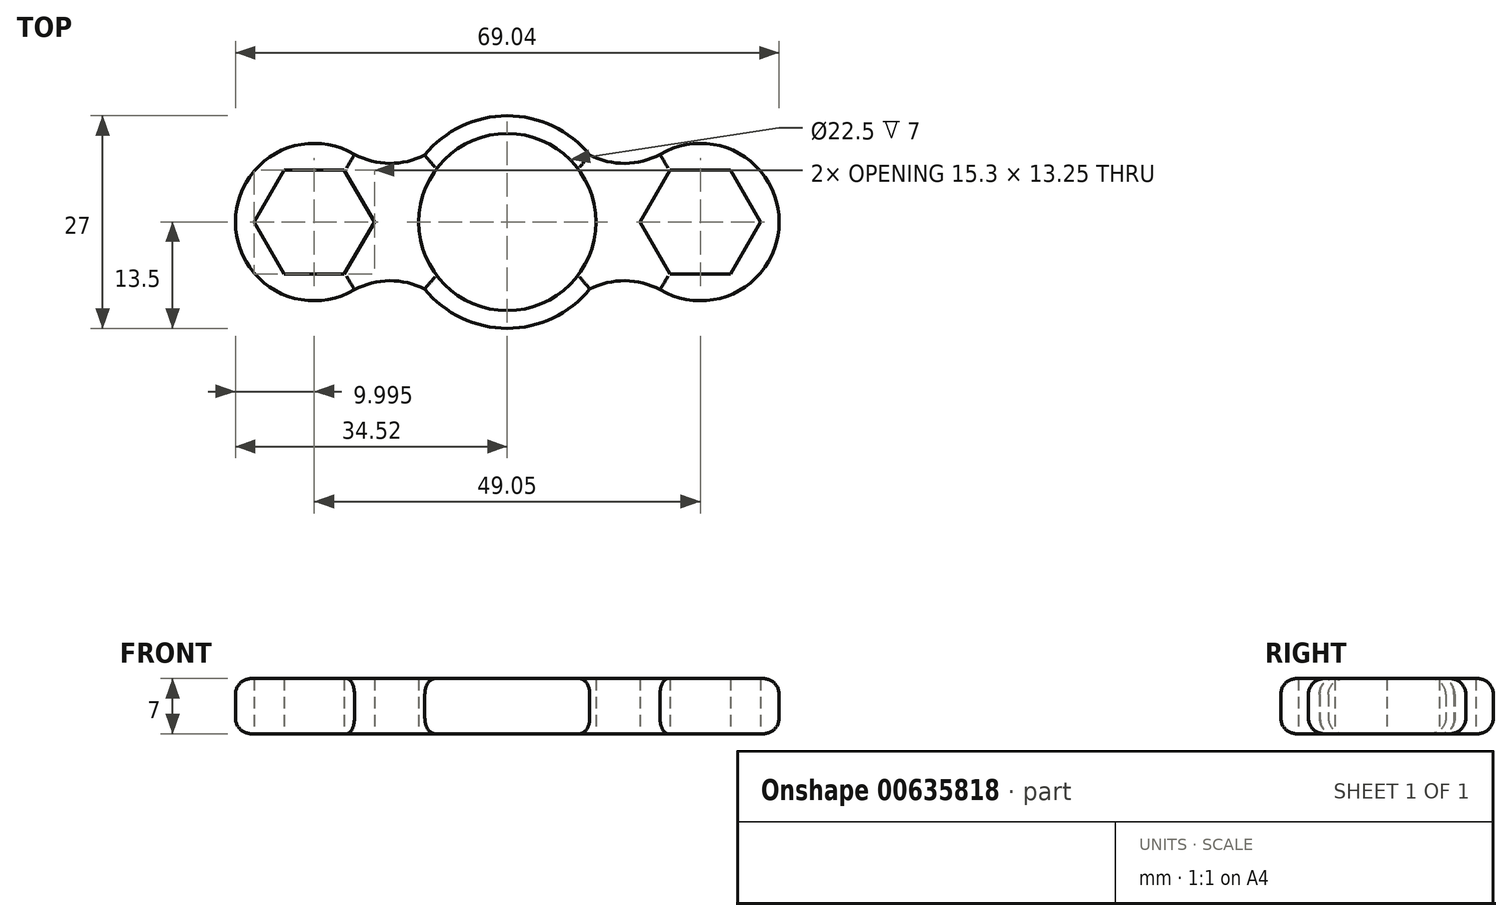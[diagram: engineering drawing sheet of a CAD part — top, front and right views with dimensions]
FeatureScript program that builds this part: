
annotation { "Feature Type Name" : "Feature", "Feature Type Description" : "" }
export const myFeature = defineFeature(function(context is Context, id is Id, definition is map)
    precondition{}
    {
        {
            var Q0;
            Q0=qCreatedBy(makeId("Top.planeOp"),FACE);
            var sketch = newSketch(context, id + "F0", { "sketchPlane" : qUnion([Q0])});
            skCircle(sketch, "E0", {"center": v(0, 0) * mm, "radius": 11.25 * mm});
            skCircle(sketch, "E1", {"center": v(24.52, 0) * mm, "radius": 10 * mm});
            skCircle(sketch, "E2", {"center": v(0, 0) * mm, "radius": 13.5 * mm});
            skPoint(sketch, "E3.center", {"position": v(-1.17, 0) * mm});
            skCircle(sketch, "E4.cCircle", {"center": v(24.52, 0) * mm, "radius": 6.62 * mm, "construction": true});
            skLineSegment(sketch, "E4.0", {"start": v(20.7, 6.63) * mm, "end": v(28.35, 6.63) * mm});
            skLineSegment(sketch, "E4.1", {"start": v(28.35, 6.62) * mm, "end": v(32.17, 0) * mm});
            skLineSegment(sketch, "E4.2", {"start": v(32.17, 0) * mm, "end": v(28.35, -6.62) * mm});
            skLineSegment(sketch, "E4.3", {"start": v(28.35, -6.62) * mm, "end": v(20.7, -6.62) * mm});
            skLineSegment(sketch, "E4.4", {"start": v(20.7, -6.63) * mm, "end": v(16.87, 0) * mm});
            skLineSegment(sketch, "E4.5", {"start": v(16.87, 0) * mm, "end": v(20.7, 6.62) * mm});
            skPoint(sketch, "E4.0.midPoint", {"position": v(24.52, 6.63) * mm});
            skLineSegment(sketch, "E5.MirrorCS", {"start": v(-16.87, 0) * mm, "end": v(-20.7, 6.62) * mm});
            skPoint(sketch, "E6.MirrorP", {"position": v(-24.52, 6.63) * mm});
            skCircle(sketch, "E7.MirrorC", {"center": v(-24.52, 0) * mm, "radius": 10 * mm});
            skCircle(sketch, "E8.MirrorC", {"center": v(-24.52, 0) * mm, "radius": 6.62 * mm, "construction": true});
            skLineSegment(sketch, "E9.MirrorCS", {"start": v(-32.17, 0) * mm, "end": v(-28.35, -6.62) * mm});
            skLineSegment(sketch, "E10.MirrorCS", {"start": v(-28.35, -6.63) * mm, "end": v(-20.7, -6.63) * mm});
            skLineSegment(sketch, "E11.MirrorCS", {"start": v(-20.7, 6.63) * mm, "end": v(-28.35, 6.63) * mm});
            skLineSegment(sketch, "E12.MirrorCS", {"start": v(-28.35, 6.62) * mm, "end": v(-32.17, 0) * mm});
            skLineSegment(sketch, "E13.MirrorCS", {"start": v(-20.7, -6.63) * mm, "end": v(-16.87, 0) * mm});
            skLineSegment(sketch, "E14", {"start": v(0, 0) * mm, "end": v(40.83, 0) * mm, "construction": true});
            skArc(sketch, "E15", {"start": v(19.41, -8.6) * mm, "mid": v(14.95, -7.45) * mm, "end": v(10.48, -8.51) * mm});
            skArc(sketch, "E16.MirrorCS", {"start": v(19.41, 8.6) * mm, "mid": v(14.95, 7.45) * mm, "end": v(10.48, 8.51) * mm});
            skArc(sketch, "E17.MirrorCS", {"start": v(-19.41, 8.6) * mm, "mid": v(-14.95, 7.45) * mm, "end": v(-10.48, 8.51) * mm});
            skArc(sketch, "E18.MirrorCS", {"start": v(-19.41, -8.6) * mm, "mid": v(-14.95, -7.45) * mm, "end": v(-10.48, -8.51) * mm});
            skSolve(sketch);
        }
        {
            var Q0;
            Q0=makeQuery(id+"F0.imprint","IMPRINT",FACE,{"disambiguationData":[TD([[makeQuery(id+"F0.imprint","IMPRINT",EDGE,{"derivedFrom":sQuery(id+"F0.wireOp",EDGE,"E4.0")}),1.0]])]});
            var Q1;
            {var subQ0=sQuery(id+"F0.wireOp",EDGE,"E17.MirrorCS");var subQ1=sQuery(id+"F0.wireOp",EDGE,"E2");var subQ2=makeQuery(id+"F0.imprint","INTERSECT",VERTEX,{"derivedFrom":[subQ1,subQ0]});Q1=makeQuery(id+"F0.imprint","IMPRINT",FACE,{"disambiguationData":[TD([[makeQuery(id+"F0.imprint","IMPRINT",EDGE,{"disambiguationData":[TD([[subQ2,-1.0]])],"derivedFrom":subQ1}),-1.0]])]});}
            var Q2;
            Q2=makeQuery(id+"F0.imprint","IMPRINT",FACE,{"disambiguationData":[TD([[makeQuery(id+"F0.imprint","IMPRINT",EDGE,{"derivedFrom":sQuery(id+"F0.wireOp",EDGE,"E0")}),-1.0]])]});
            var Q3;
            {var subQ0=sQuery(id+"F0.wireOp",EDGE,"E16.MirrorCS");var subQ1=sQuery(id+"F0.wireOp",EDGE,"E1");var subQ2=makeQuery(id+"F0.imprint","INTERSECT",VERTEX,{"disambiguationData":[OD(1.0)],"derivedFrom":[subQ1,subQ0]});Q3=makeQuery(id+"F0.imprint","IMPRINT",FACE,{"disambiguationData":[TD([[makeQuery(id+"F0.imprint","IMPRINT",EDGE,{"disambiguationData":[TD([[subQ2,-1.0]])],"derivedFrom":subQ1}),-1.0]])]});}
            var Q4;
            Q4=makeQuery(id+"F0.imprint","IMPRINT",FACE,{"disambiguationData":[TD([[makeQuery(id+"F0.imprint","IMPRINT",EDGE,{"derivedFrom":sQuery(id+"F0.wireOp",EDGE,"E10.MirrorCS")}),-1.0]])]});
            var Q5;
            {var subQ0=sQuery(id+"F0.wireOp",EDGE,"E16.MirrorCS");var subQ1=sQuery(id+"F0.wireOp",EDGE,"E1");var subQ2=makeQuery(id+"F0.imprint","INTERSECT",VERTEX,{"disambiguationData":[OD(0.0)],"derivedFrom":[subQ1,subQ0]});Q5=makeQuery(id+"F0.imprint","IMPRINT",FACE,{"disambiguationData":[TD([[makeQuery(id+"F0.imprint","IMPRINT",EDGE,{"disambiguationData":[TD([[subQ2,-1.0]])],"derivedFrom":subQ1}),1.0]])]});}
            var Q6;
            {var subQ0=sQuery(id+"F0.wireOp",EDGE,"E15");var subQ1=sQuery(id+"F0.wireOp",EDGE,"E1");var subQ2=makeQuery(id+"F0.imprint","INTERSECT",VERTEX,{"disambiguationData":[OD(0.0)],"derivedFrom":[subQ1,subQ0]});Q6=makeQuery(id+"F0.imprint","IMPRINT",FACE,{"disambiguationData":[TD([[makeQuery(id+"F0.imprint","IMPRINT",EDGE,{"disambiguationData":[TD([[subQ2,1.0]])],"derivedFrom":subQ1}),1.0]])]});}
            var Q7;
            {var subQ0=sQuery(id+"F0.wireOp",EDGE,"E18.MirrorCS");var subQ1=sQuery(id+"F0.wireOp",EDGE,"E7.MirrorC");var subQ2=makeQuery(id+"F0.imprint","INTERSECT",VERTEX,{"disambiguationData":[OD(0.0)],"derivedFrom":[subQ1,subQ0]});Q7=makeQuery(id+"F0.imprint","IMPRINT",FACE,{"disambiguationData":[TD([[makeQuery(id+"F0.imprint","IMPRINT",EDGE,{"disambiguationData":[TD([[subQ2,1.0]])],"derivedFrom":subQ1}),-1.0]])]});}
            var Q8;
            {var subQ0=sQuery(id+"F0.wireOp",EDGE,"E17.MirrorCS");var subQ1=sQuery(id+"F0.wireOp",EDGE,"E7.MirrorC");var subQ2=makeQuery(id+"F0.imprint","INTERSECT",VERTEX,{"disambiguationData":[OD(0.0)],"derivedFrom":[subQ1,subQ0]});Q8=makeQuery(id+"F0.imprint","IMPRINT",FACE,{"disambiguationData":[TD([[makeQuery(id+"F0.imprint","IMPRINT",EDGE,{"disambiguationData":[TD([[subQ2,-1.0]])],"derivedFrom":subQ1}),-1.0]])]});}
            extrude(context, id + "F1", {"entities" : qUnion([Q0, Q1, Q2, Q3, Q4, Q5, Q6, Q7, Q8]), "depth" : 7 * mm, "offsetDistance" : 25 * mm});
        }
        {
            var Q0;
            Q0=makeQuery(id+"F1.opExtrude","CAP_EDGE",EDGE,{"disambiguationData":[OSD([sQuery(id+"F0.wireOp",EDGE,"E7.MirrorC")])],"isStart":false});
            var Q1;
            {var subQ0=sQuery(id+"F0.wireOp",EDGE,"E2");Q1=makeQuery(id+"F1.opExtrude","CAP_EDGE",EDGE,{"disambiguationData":[OSD([subQ0]),TDD([makeQuery(id+"F0.imprint","IMPRINT",EDGE,{"disambiguationData":[TD([[makeQuery(id+"F0.imprint","INTERSECT",VERTEX,{"derivedFrom":[subQ0,sQuery(id+"F0.wireOp",EDGE,"E15")]}),1.0]])],"derivedFrom":subQ0})])],"isStart":false});}
            var Q2;
            Q2=makeQuery(id+"F1.opExtrude","CAP_EDGE",EDGE,{"disambiguationData":[OSD([sQuery(id+"F0.wireOp",EDGE,"E15")])],"isStart":false});
            var Q3;
            Q3=makeQuery(id+"F1.opExtrude","CAP_EDGE",EDGE,{"disambiguationData":[OSD([sQuery(id+"F0.wireOp",EDGE,"E1")])],"isStart":false});
            var Q4;
            Q4=makeQuery(id+"F1.opExtrude","CAP_EDGE",EDGE,{"disambiguationData":[OSD([sQuery(id+"F0.wireOp",EDGE,"E16.MirrorCS")])],"isStart":false});
            var Q5;
            {var subQ0=sQuery(id+"F0.wireOp",EDGE,"E2");Q5=makeQuery(id+"F1.opExtrude","CAP_EDGE",EDGE,{"disambiguationData":[OSD([subQ0]),TDD([makeQuery(id+"F0.imprint","IMPRINT",EDGE,{"disambiguationData":[TD([[makeQuery(id+"F0.imprint","INTERSECT",VERTEX,{"derivedFrom":[subQ0,sQuery(id+"F0.wireOp",EDGE,"E16.MirrorCS")]}),-1.0]])],"derivedFrom":subQ0})])],"isStart":false});}
            var Q6;
            Q6=makeQuery(id+"F1.opExtrude","CAP_EDGE",EDGE,{"disambiguationData":[OSD([sQuery(id+"F0.wireOp",EDGE,"E15")])],"isStart":true});
            var Q7;
            {var subQ0=sQuery(id+"F0.wireOp",EDGE,"E2");Q7=makeQuery(id+"F1.opExtrude","CAP_EDGE",EDGE,{"disambiguationData":[OSD([subQ0]),TDD([makeQuery(id+"F0.imprint","IMPRINT",EDGE,{"disambiguationData":[TD([[makeQuery(id+"F0.imprint","INTERSECT",VERTEX,{"derivedFrom":[subQ0,sQuery(id+"F0.wireOp",EDGE,"E15")]}),1.0]])],"derivedFrom":subQ0})])],"isStart":true});}
            var Q8;
            Q8=makeQuery(id+"F1.opExtrude","CAP_EDGE",EDGE,{"disambiguationData":[OSD([sQuery(id+"F0.wireOp",EDGE,"E18.MirrorCS")])],"isStart":true});
            var Q9;
            Q9=makeQuery(id+"F1.opExtrude","CAP_EDGE",EDGE,{"disambiguationData":[OSD([sQuery(id+"F0.wireOp",EDGE,"E7.MirrorC")])],"isStart":true});
            var Q10;
            Q10=makeQuery(id+"F1.opExtrude","CAP_EDGE",EDGE,{"disambiguationData":[OSD([sQuery(id+"F0.wireOp",EDGE,"E17.MirrorCS")])],"isStart":true});
            var Q11;
            {var subQ0=sQuery(id+"F0.wireOp",EDGE,"E2");Q11=makeQuery(id+"F1.opExtrude","CAP_EDGE",EDGE,{"disambiguationData":[OSD([subQ0]),TDD([makeQuery(id+"F0.imprint","IMPRINT",EDGE,{"disambiguationData":[TD([[makeQuery(id+"F0.imprint","INTERSECT",VERTEX,{"derivedFrom":[subQ0,sQuery(id+"F0.wireOp",EDGE,"E16.MirrorCS")]}),-1.0]])],"derivedFrom":subQ0})])],"isStart":true});}
            var Q12;
            Q12=makeQuery(id+"F1.opExtrude","CAP_EDGE",EDGE,{"disambiguationData":[OSD([sQuery(id+"F0.wireOp",EDGE,"E16.MirrorCS")])],"isStart":true});
            var Q13;
            Q13=makeQuery(id+"F1.opExtrude","CAP_EDGE",EDGE,{"disambiguationData":[OSD([sQuery(id+"F0.wireOp",EDGE,"E1")])],"isStart":true});
            fillet(context, id + "F2", {"entities" : qUnion([Q0, Q1, Q2, Q3, Q4, Q5, Q6, Q7, Q8, Q9, Q10, Q11, Q12, Q13]), "radius" : 2 * mm, "tangentPropagation" : true, "allowEdgeOverflow" : false});
        }
    });
